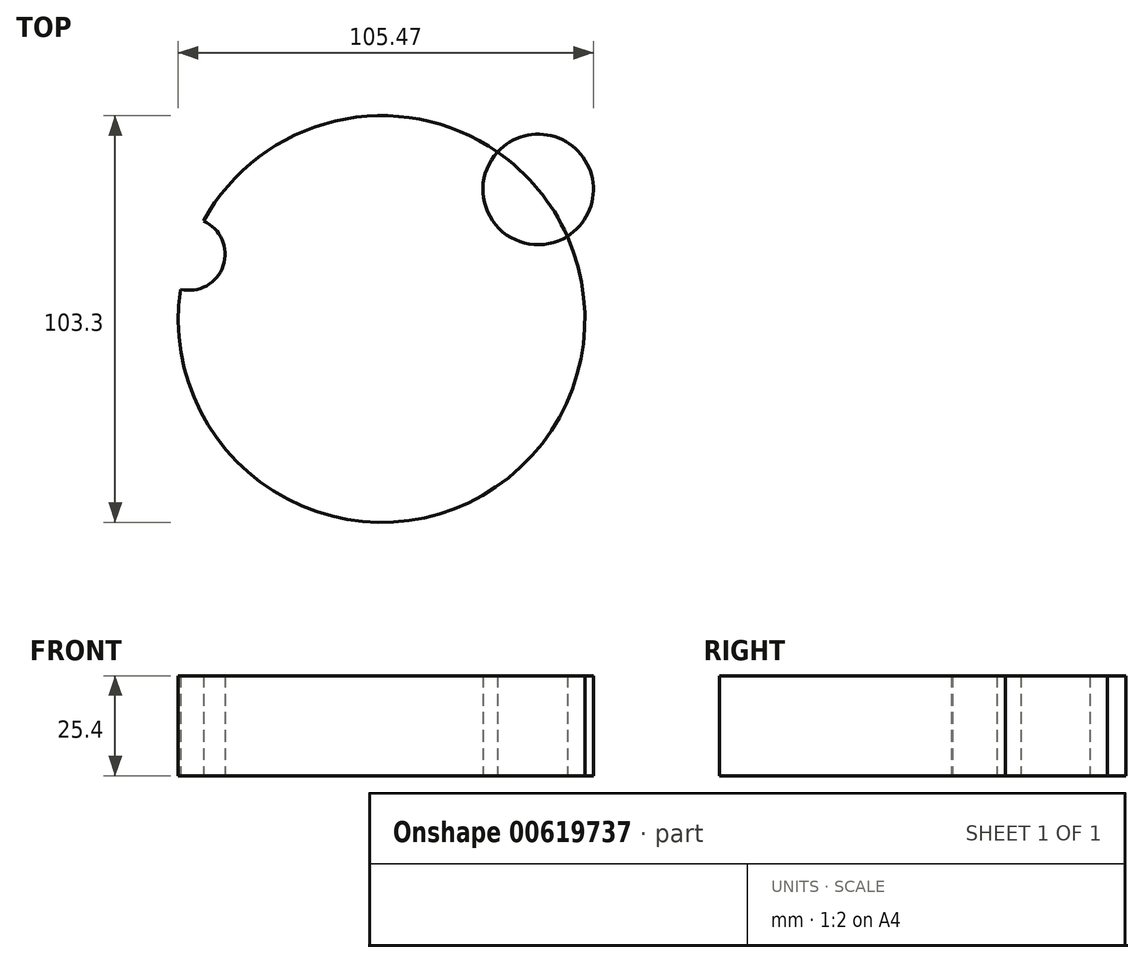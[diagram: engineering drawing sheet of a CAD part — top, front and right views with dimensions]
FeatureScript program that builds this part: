
annotation { "Feature Type Name" : "Feature", "Feature Type Description" : "" }
export const myFeature = defineFeature(function(context is Context, id is Id, definition is map)
    precondition{}
    {
        {
            var Q0;
            Q0=qCreatedBy(makeId("Top.planeOp"),FACE);
            var sketch = newSketch(context, id + "F0", { "sketchPlane" : qUnion([Q0])});
            skCircle(sketch, "E0", {"center": v(0, 0) * mm, "radius": 51.65 * mm});
            skCircle(sketch, "E1", {"center": v(-48.95, 16.49) * mm, "radius": 9.2 * mm});
            skCircle(sketch, "E2", {"center": v(39.78, 32.94) * mm, "radius": 14.04 * mm});
            skSolve(sketch);
        }
        {
            var Q0;
            {var subQ0=sQuery(id+"F0.wireOp",EDGE,"E2");var subQ1=sQuery(id+"F0.wireOp",EDGE,"E0");var subQ2=makeQuery(id+"F0.imprint","INTERSECT",VERTEX,{"disambiguationData":[OD(0.0)],"derivedFrom":[subQ1,subQ0]});Q0=makeQuery(id+"F0.imprint","IMPRINT",FACE,{"disambiguationData":[TD([[makeQuery(id+"F0.imprint","IMPRINT",EDGE,{"disambiguationData":[TD([[subQ2,-1.0]])],"derivedFrom":subQ1}),1.0]])]});}
            var Q1;
            {var subQ0=sQuery(id+"F0.wireOp",EDGE,"E2");var subQ1=sQuery(id+"F0.wireOp",EDGE,"E0");var subQ2=makeQuery(id+"F0.imprint","INTERSECT",VERTEX,{"disambiguationData":[OD(0.0)],"derivedFrom":[subQ1,subQ0]});Q1=makeQuery(id+"F0.imprint","IMPRINT",FACE,{"disambiguationData":[TD([[makeQuery(id+"F0.imprint","IMPRINT",EDGE,{"disambiguationData":[TD([[subQ2,1.0]])],"derivedFrom":subQ1}),-1.0]])]});}
            extrude(context, id + "F1", {"entities" : qUnion([Q0, Q1]), "depth" : 25.4 * mm, "offsetDistance" : 25.4 * mm});
        }
    });
